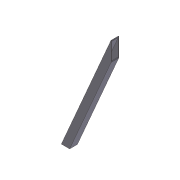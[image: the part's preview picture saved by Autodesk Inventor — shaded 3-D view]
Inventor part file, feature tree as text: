
AUTODESK INVENTOR PART (.ipt)
format: ipt  version: 2012 (Build 160160000, 160)  size: 74,752 bytes
history: native  units: in
note: dims shown in document units (in); Inventor stores cm internally (conversion verified against a paired STEP export)
features: extrude x1, shell x1, sketch x1
ambient origin geometry x8: Origin, YZ Plane, XZ Plane, XY Plane, X Axis, Y Axis, Z Axis, Center Point
bodies: Solid1 (feature_tree)
feature tree (3):
  extrude  "Extrusion1"  Depth=1.0in
  shell  "Shell1"  Thickness=6.5in
  sketch  "Sketch1"  dims[d0=15.0in d2=1.0in d3=6.5in d4=1.0in d5=0.0in d6=0.0625in]
